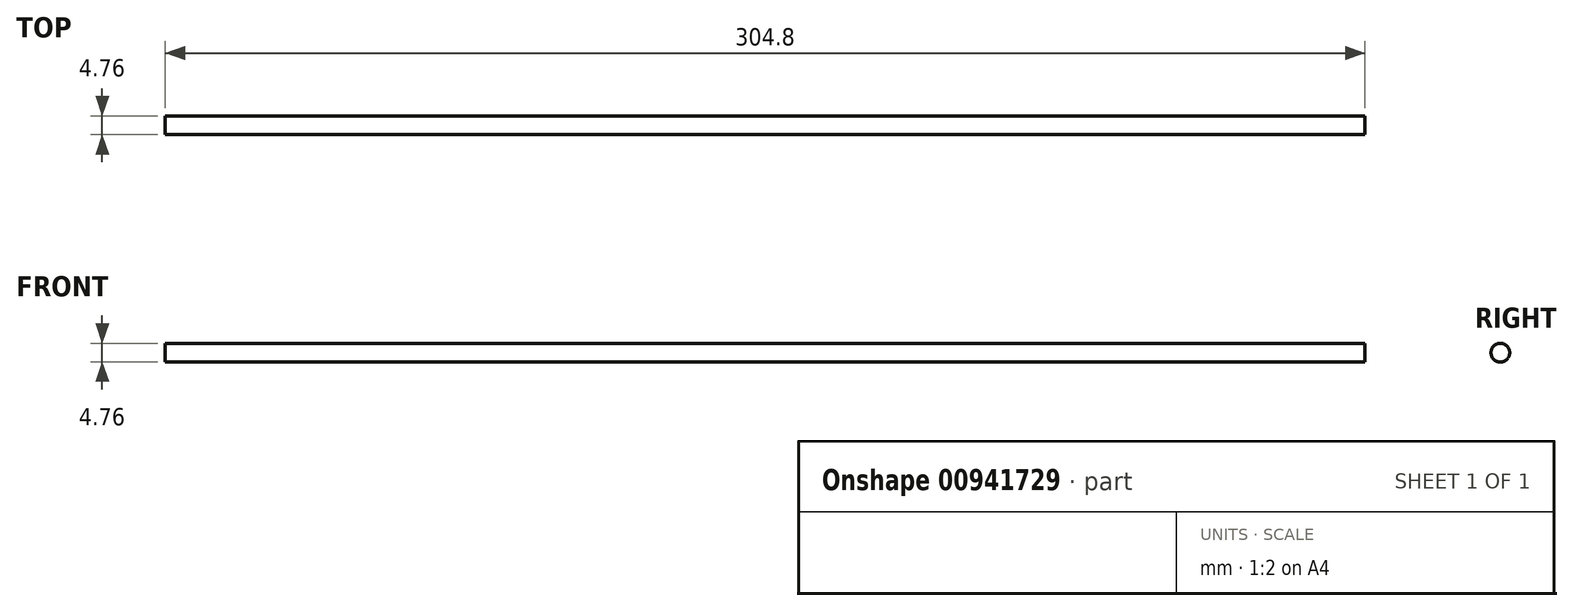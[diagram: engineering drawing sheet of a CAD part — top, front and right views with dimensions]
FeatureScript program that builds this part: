
annotation { "Feature Type Name" : "Feature", "Feature Type Description" : "" }
export const myFeature = defineFeature(function(context is Context, id is Id, definition is map)
    precondition{}
    {
        {
            var Q0;
            Q0=qCreatedBy(makeId("Right.planeOp"),FACE);
            var sketch = newSketch(context, id + "F0", { "sketchPlane" : qUnion([Q0])});
            skCircle(sketch, "E0", {"center": v(-26.41, 0) * mm, "radius": 2.38 * mm});
            skSolve(sketch);
        }
        {
            var Q0;
            Q0=sQuery(id+"F0.wireOp",EDGE,"E0");
            extrude(context, id + "F1", {"bodyType" : ToolBodyType.SURFACE, "surfaceEntities" : qUnion([Q0]), "depth" : 304.8 * mm, "offsetDistance" : 25.4 * mm});
        }
    });
